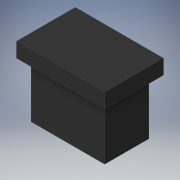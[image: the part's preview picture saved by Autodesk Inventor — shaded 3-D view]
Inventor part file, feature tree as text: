
AUTODESK INVENTOR PART (.ipt)
format: ipt  version: 2019 (Build 230136000, 136)  size: 108,544 bytes
history: native  units: mm
features: extrude x2, sketch x2
ambient origin geometry x8: Origin, YZ Plane, XZ Plane, XY Plane, X Axis, Y Axis, Z Axis, Center Point
bodies: Solid1 (feature_tree)
feature tree (4):
  extrude  "Extrusion1"  Depth=12.0mm
  extrude  "Extrusion2"  Depth=2.0mm
  sketch  "Sketch1"  dims[d0=20.0mm d1=12.0mm]
  sketch  "Sketch2"  dims[d2=15.0mm d3=0.0mm d4=2.0mm d5=2.0mm d6=4.0mm d7=0.0mm]
